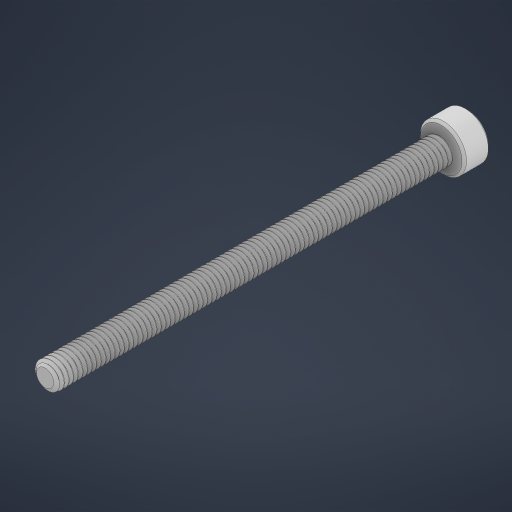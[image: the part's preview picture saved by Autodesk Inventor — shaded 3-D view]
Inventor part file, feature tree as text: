
AUTODESK INVENTOR PART (.ipt)
format: ipt  version: 2023 (Build 270158000, 158)  size: 2,142,720 bytes
history: native  units: in
note: dims shown in document units (in); Inventor stores cm internally (conversion verified against a paired STEP export)
features: chamfer x1
ambient origin geometry x8: Origin, YZ Plane, XZ Plane, XY Plane, X Axis, Y Axis, Z Axis, Center Point
bodies: Solid1 (feature_tree)
feature tree (1):
  chamfer  "Chamfer1"  [1 undecoded]
note: 1 required parameter value undecoded (feature->parameter linkage not recoverable at this tier; creation-order binding heuristic only, values carry confidence <= 0.55)
